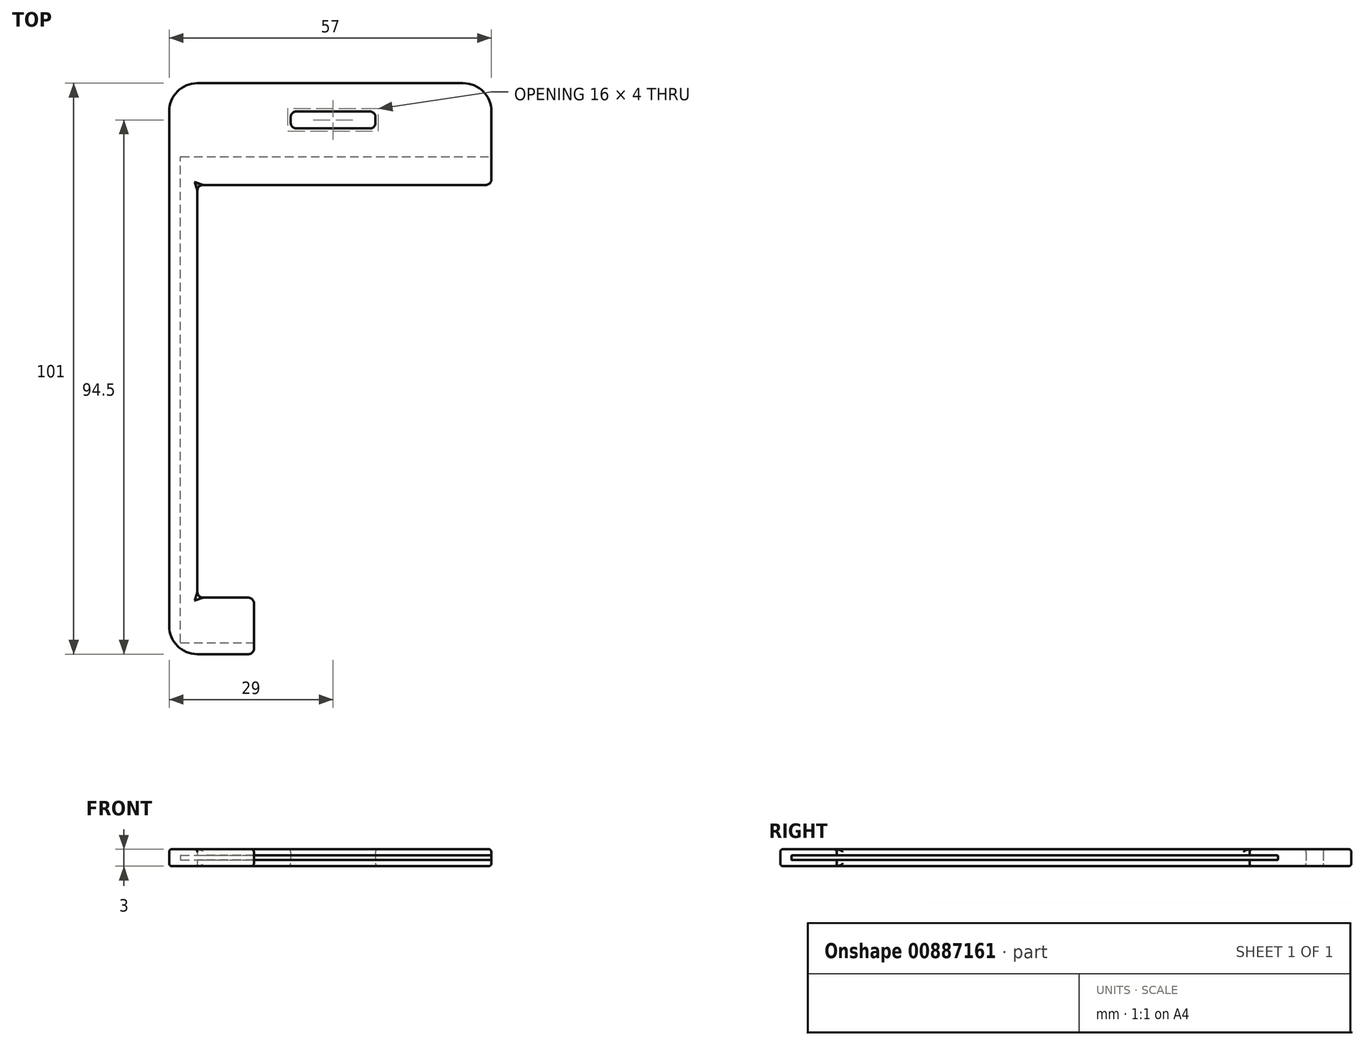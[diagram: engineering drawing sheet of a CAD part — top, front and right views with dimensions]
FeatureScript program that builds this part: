
annotation { "Feature Type Name" : "Feature", "Feature Type Description" : "" }
export const myFeature = defineFeature(function(context is Context, id is Id, definition is map)
    precondition{}
    {
        {
            var Q0;
            Q0=qCreatedBy(makeId("Top.planeOp"),FACE);
            var sketch = newSketch(context, id + "F0", { "sketchPlane" : qUnion([Q0])});
            skLineSegment(sketch, "E0", {"start": v(28, 18) * mm, "end": v(-29, 18) * mm});
            skLineSegment(sketch, "E1", {"start": v(-29, 18) * mm, "end": v(-29, -83) * mm});
            skLineSegment(sketch, "E2", {"start": v(-29, -83) * mm, "end": v(-14, -83) * mm});
            skLineSegment(sketch, "E3", {"start": v(-14, -83) * mm, "end": v(-14, -73) * mm});
            skLineSegment(sketch, "E4", {"start": v(-14, -73) * mm, "end": v(-24, -73) * mm});
            skLineSegment(sketch, "E5", {"start": v(-24, -73) * mm, "end": v(-24, 0) * mm});
            skLineSegment(sketch, "E6", {"start": v(-24, 0) * mm, "end": v(28, 0) * mm});
            skLineSegment(sketch, "E7", {"start": v(28, 0) * mm, "end": v(28, 18) * mm});
            skLineSegment(sketch, "E8.bottom", {"start": v(-7.5, 13) * mm, "end": v(7.5, 13) * mm});
            skLineSegment(sketch, "E8.top", {"start": v(-7.5, 10) * mm, "end": v(7.5, 10) * mm});
            skLineSegment(sketch, "E8.left", {"start": v(-7.5, 13) * mm, "end": v(-7.5, 10) * mm});
            skLineSegment(sketch, "E8.right", {"start": v(7.5, 13) * mm, "end": v(7.5, 10) * mm});
            skLineSegment(sketch, "E9", {"start": v(0, 10) * mm, "end": v(0, 0) * mm, "construction": true});
            skLineSegment(sketch, "E10", {"start": v(27, 5) * mm, "end": v(-27, 5) * mm, "construction": true});
            skLineSegment(sketch, "E11", {"start": v(-27, -81) * mm, "end": v(-27, 5) * mm, "construction": true});
            skLineSegment(sketch, "E12", {"start": v(-27, -81) * mm, "end": v(-14, -81) * mm, "construction": true});
            skSolve(sketch);
        }
        {
            var Q0;
            Q0=makeQuery(id+"F0.imprint","IMPRINT",FACE,{"disambiguationData":[TD([[makeQuery(id+"F0.imprint","IMPRINT",EDGE,{"derivedFrom":sQuery(id+"F0.wireOp",EDGE,"E0")}),1.0]])]});
            extrude(context, id + "F1", {"entities" : qUnion([Q0]), "depth" : 3 * mm, "offsetDistance" : 25 * mm});
        }
        {
            var Q0;
            Q0=makeQuery(id+"F1.opExtrude","SWEPT_EDGE",EDGE,{"disambiguationData":[OSD([sQuery(id+"F0.wireOp",EDGE,"E0"),sQuery(id+"F0.wireOp",EDGE,"E7")])]});
            var Q1;
            Q1=makeQuery(id+"F1.opExtrude","SWEPT_EDGE",EDGE,{"disambiguationData":[OSD([sQuery(id+"F0.wireOp",EDGE,"E0"),sQuery(id+"F0.wireOp",EDGE,"E1")])]});
            var Q2;
            Q2=makeQuery(id+"F1.opExtrude","SWEPT_EDGE",EDGE,{"disambiguationData":[OSD([sQuery(id+"F0.wireOp",EDGE,"E1"),sQuery(id+"F0.wireOp",EDGE,"E2")])]});
            fillet(context, id + "F2", {"entities" : qUnion([Q0, Q1, Q2]), "radius" : 5 * mm, "tangentPropagation" : true, "allowEdgeOverflow" : false});
        }
        {
            var Q0;
            Q0=makeQuery(id+"F1.opExtrude","SWEPT_EDGE",EDGE,{"disambiguationData":[OSD([sQuery(id+"F0.wireOp",EDGE,"E8.bottom"),sQuery(id+"F0.wireOp",EDGE,"E8.left")])]});
            var Q1;
            Q1=makeQuery(id+"F1.opExtrude","SWEPT_EDGE",EDGE,{"disambiguationData":[OSD([sQuery(id+"F0.wireOp",EDGE,"E8.top"),sQuery(id+"F0.wireOp",EDGE,"E8.left")])]});
            var Q2;
            Q2=makeQuery(id+"F1.opExtrude","SWEPT_EDGE",EDGE,{"disambiguationData":[OSD([sQuery(id+"F0.wireOp",EDGE,"E8.top"),sQuery(id+"F0.wireOp",EDGE,"E8.right")])]});
            var Q3;
            Q3=makeQuery(id+"F1.opExtrude","SWEPT_EDGE",EDGE,{"disambiguationData":[OSD([sQuery(id+"F0.wireOp",EDGE,"E8.bottom"),sQuery(id+"F0.wireOp",EDGE,"E8.right")])]});
            fillet(context, id + "F3", {"entities" : qUnion([Q0, Q1, Q2, Q3]), "radius" : 1 * mm, "tangentPropagation" : true, "allowEdgeOverflow" : false});
        }
        {
            var Q0;
            Q0=makeQuery(id+"F1.opExtrude","SWEPT_FACE",FACE,{"disambiguationData":[OSD([sQuery(id+"F0.wireOp",EDGE,"E7")])]});
            var sketch = newSketch(context, id + "F4", { "sketchPlane" : qUnion([Q0])});
            skLineSegment(sketch, "E13.bottom", {"start": v(-81, 1.92) * mm, "end": v(5, 1.93) * mm});
            skLineSegment(sketch, "E13.top", {"start": v(-81, 1.07) * mm, "end": v(5, 1.08) * mm});
            skLineSegment(sketch, "E13.left", {"start": v(-81, 1.92) * mm, "end": v(-81, 1.07) * mm});
            skLineSegment(sketch, "E13.right", {"start": v(5, 1.92) * mm, "end": v(5, 1.08) * mm});
            skLineSegment(sketch, "E14", {"start": v(0, 1.5) * mm, "end": v(5, 1.5) * mm, "construction": true});
            skSolve(sketch);
        }
        {
            var Q0;
            {var subQ0=sQuery(id+"F4.wireOp",EDGE,"E13.left");Q0=makeQuery(id+"F4.imprint","IMPRINT",FACE,{"disambiguationData":[TD([[makeQuery(id+"F4.imprint","IMPRINT",EDGE,{"derivedFrom":subQ0}),1.0]])]});}
            var Q1;
            {var subQ0=sQuery(id+"F4.wireOp",EDGE,"E13.right");Q1=makeQuery(id+"F4.imprint","IMPRINT",FACE,{"disambiguationData":[TD([[makeQuery(id+"F4.imprint","IMPRINT",EDGE,{"derivedFrom":subQ0}),-1.0]])]});}
            extrude(context, id + "F5", {"entities" : qUnion([Q0, Q1]), "operationType" : NewBodyOperationType.REMOVE, "oppositeDirection" : true, "depth" : 55 * mm, "offsetDistance" : 25 * mm});
        }
        {
            var Q0;
            Q0=makeQuery(id+"F1.opExtrude","CAP_EDGE",EDGE,{"disambiguationData":[OSD([sQuery(id+"F0.wireOp",EDGE,"E8.bottom")])],"isStart":false});
            var Q1;
            Q1=makeQuery(id+"F1.opExtrude","CAP_FACE",FACE,{"disambiguationData":[OSD([sQuery(id+"F0.wireOp",EDGE,"E0"),sQuery(id+"F0.wireOp",EDGE,"E1"),sQuery(id+"F0.wireOp",EDGE,"E2"),sQuery(id+"F0.wireOp",EDGE,"E3"),sQuery(id+"F0.wireOp",EDGE,"E4"),sQuery(id+"F0.wireOp",EDGE,"E5"),sQuery(id+"F0.wireOp",EDGE,"E6"),sQuery(id+"F0.wireOp",EDGE,"E7"),sQuery(id+"F0.wireOp",EDGE,"E8.bottom"),sQuery(id+"F0.wireOp",EDGE,"E8.top"),sQuery(id+"F0.wireOp",EDGE,"E8.left"),sQuery(id+"F0.wireOp",EDGE,"E8.right")])],"isStart":false});
            var Q2;
            Q2=makeQuery(id+"F1.opExtrude","CAP_FACE",FACE,{"disambiguationData":[OSD([sQuery(id+"F0.wireOp",EDGE,"E0"),sQuery(id+"F0.wireOp",EDGE,"E1"),sQuery(id+"F0.wireOp",EDGE,"E2"),sQuery(id+"F0.wireOp",EDGE,"E3"),sQuery(id+"F0.wireOp",EDGE,"E4"),sQuery(id+"F0.wireOp",EDGE,"E5"),sQuery(id+"F0.wireOp",EDGE,"E6"),sQuery(id+"F0.wireOp",EDGE,"E7"),sQuery(id+"F0.wireOp",EDGE,"E8.bottom"),sQuery(id+"F0.wireOp",EDGE,"E8.top"),sQuery(id+"F0.wireOp",EDGE,"E8.left"),sQuery(id+"F0.wireOp",EDGE,"E8.right")])],"isStart":true});
            fillet(context, id + "F6", {"entities" : qUnion([Q0, Q1, Q2]), "radius" : .5 * mm, "tangentPropagation" : true, "allowEdgeOverflow" : false});
        }
        {
            var Q0;
            {var subQ0=sQuery(id+"F0.wireOp",EDGE,"E6");var subQ1=sQuery(id+"F0.wireOp",EDGE,"E5");Q0=makeQuery(id+"F5.boolean.opBoolean","SPLIT",EDGE,{"disambiguationData":[TD([makeQuery(id+"F5.opExtrude","SWEPT_FACE",FACE,{"disambiguationData":[OSD([sQuery(id+"F4.wireOp",EDGE,"E13.bottom")])]})])],"derivedFrom":makeQuery(id+"F1.opExtrude","SWEPT_EDGE",EDGE,{"disambiguationData":[OSD([subQ1,subQ0])]})});}
            var Q1;
            {var subQ0=sQuery(id+"F0.wireOp",EDGE,"E7");var subQ1=sQuery(id+"F0.wireOp",EDGE,"E6");Q1=makeQuery(id+"F5.boolean.opBoolean","SPLIT",EDGE,{"disambiguationData":[TD([makeQuery(id+"F5.opExtrude","SWEPT_FACE",FACE,{"disambiguationData":[OSD([sQuery(id+"F4.wireOp",EDGE,"E13.bottom")])]})])],"derivedFrom":makeQuery(id+"F1.opExtrude","SWEPT_EDGE",EDGE,{"disambiguationData":[OSD([subQ1,subQ0])]})});}
            var Q2;
            {var subQ0=sQuery(id+"F0.wireOp",EDGE,"E7");var subQ1=sQuery(id+"F0.wireOp",EDGE,"E6");Q2=makeQuery(id+"F5.boolean.opBoolean","SPLIT",EDGE,{"disambiguationData":[TD([makeQuery(id+"F5.opExtrude","SWEPT_FACE",FACE,{"disambiguationData":[OSD([sQuery(id+"F4.wireOp",EDGE,"E13.top")])]})])],"derivedFrom":makeQuery(id+"F1.opExtrude","SWEPT_EDGE",EDGE,{"disambiguationData":[OSD([subQ1,subQ0])]})});}
            var Q3;
            {var subQ0=sQuery(id+"F0.wireOp",EDGE,"E5");var subQ1=sQuery(id+"F0.wireOp",EDGE,"E4");Q3=makeQuery(id+"F5.boolean.opBoolean","SPLIT",EDGE,{"disambiguationData":[TD([makeQuery(id+"F5.opExtrude","SWEPT_FACE",FACE,{"disambiguationData":[OSD([sQuery(id+"F4.wireOp",EDGE,"E13.top")])]})])],"derivedFrom":makeQuery(id+"F1.opExtrude","SWEPT_EDGE",EDGE,{"disambiguationData":[OSD([subQ1,subQ0])]})});}
            var Q4;
            {var subQ0=sQuery(id+"F0.wireOp",EDGE,"E5");var subQ1=sQuery(id+"F0.wireOp",EDGE,"E4");Q4=makeQuery(id+"F5.boolean.opBoolean","SPLIT",EDGE,{"disambiguationData":[TD([makeQuery(id+"F5.opExtrude","SWEPT_FACE",FACE,{"disambiguationData":[OSD([sQuery(id+"F4.wireOp",EDGE,"E13.bottom")])]})])],"derivedFrom":makeQuery(id+"F1.opExtrude","SWEPT_EDGE",EDGE,{"disambiguationData":[OSD([subQ1,subQ0])]})});}
            var Q5;
            {var subQ0=sQuery(id+"F0.wireOp",EDGE,"E4");var subQ1=sQuery(id+"F0.wireOp",EDGE,"E3");Q5=makeQuery(id+"F5.boolean.opBoolean","SPLIT",EDGE,{"disambiguationData":[TD([makeQuery(id+"F5.opExtrude","SWEPT_FACE",FACE,{"disambiguationData":[OSD([sQuery(id+"F4.wireOp",EDGE,"E13.bottom")])]})])],"derivedFrom":makeQuery(id+"F1.opExtrude","SWEPT_EDGE",EDGE,{"disambiguationData":[OSD([subQ1,subQ0])]})});}
            var Q6;
            {var subQ0=sQuery(id+"F0.wireOp",EDGE,"E4");var subQ1=sQuery(id+"F0.wireOp",EDGE,"E3");Q6=makeQuery(id+"F5.boolean.opBoolean","SPLIT",EDGE,{"disambiguationData":[TD([makeQuery(id+"F5.opExtrude","SWEPT_FACE",FACE,{"disambiguationData":[OSD([sQuery(id+"F4.wireOp",EDGE,"E13.top")])]})])],"derivedFrom":makeQuery(id+"F1.opExtrude","SWEPT_EDGE",EDGE,{"disambiguationData":[OSD([subQ1,subQ0])]})});}
            var Q7;
            Q7=makeQuery(id+"F1.opExtrude","SWEPT_EDGE",EDGE,{"disambiguationData":[OSD([sQuery(id+"F0.wireOp",EDGE,"E2"),sQuery(id+"F0.wireOp",EDGE,"E3")])]});
            fillet(context, id + "F7", {"entities" : qUnion([Q0, Q1, Q2, Q3, Q4, Q5, Q6, Q7]), "radius" : 1 * mm, "tangentPropagation" : true, "allowEdgeOverflow" : false});
        }
        {
            var Q0;
            Q0=makeQuery(id+"F5.boolean.opBoolean","COPY",FACE,{"derivedFrom":makeQuery(id+"F5.opExtrude","SWEPT_FACE",FACE,{"disambiguationData":[OSD([sQuery(id+"F4.wireOp",EDGE,"E13.left")])]})});
            var Q1;
            Q1=makeQuery(id+"F5.boolean.opBoolean","COPY",FACE,{"derivedFrom":makeQuery(id+"F5.opExtrude","CAP_FACE",FACE,{"disambiguationData":[OSD([sQuery(id+"F4.wireOp",EDGE,"E13.bottom"),sQuery(id+"F4.wireOp",EDGE,"E13.top"),sQuery(id+"F4.wireOp",EDGE,"E13.left"),sQuery(id+"F4.wireOp",EDGE,"E13.right")])],"isStart":false})});
            var Q2;
            Q2=makeQuery(id+"F5.boolean.opBoolean","COPY",FACE,{"derivedFrom":makeQuery(id+"F5.opExtrude","SWEPT_FACE",FACE,{"disambiguationData":[OSD([sQuery(id+"F4.wireOp",EDGE,"E13.right")])]})});
            fillet(context, id + "F8", {"entities" : qUnion([Q0, Q1, Q2]), "radius" : .1 * mm, "tangentPropagation" : true, "allowEdgeOverflow" : false});
        }
    });
